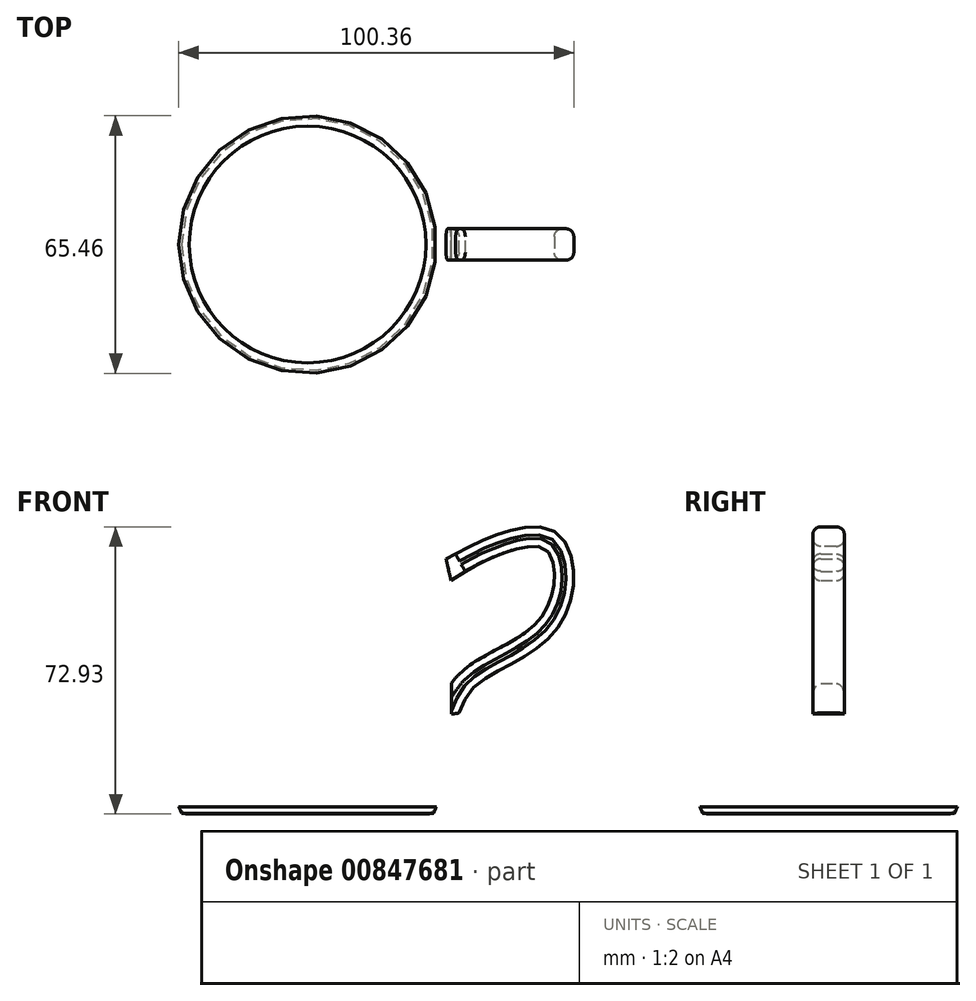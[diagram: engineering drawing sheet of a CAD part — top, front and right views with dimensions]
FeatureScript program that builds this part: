
annotation { "Feature Type Name" : "Feature", "Feature Type Description" : "" }
export const myFeature = defineFeature(function(context is Context, id is Id, definition is map)
    precondition{}
    {
        {
            var Q0;
            Q0=qCreatedBy(makeId("Front.planeOp"),FACE);
            var sketch = newSketch(context, id + "F0", { "sketchPlane" : qUnion([Q0])});
            skFitSpline(sketch, "E0", {"points": [v(0, 3) * mm, v(11.69, 2.8) * mm, v(27, 0) * mm, v(32, 0) * mm], "startDerivative": vector(30.02, 0) * mm, "endDerivative": vector(16.65, 1.68) * mm});
            skFitSpline(sketch, "E1", {"points": [v(32, 0) * mm, v(37.17, 14.97) * mm, v(38.39, 37.94) * mm, v(37.4, 75) * mm], "startDerivative": vector(17.24, 38.39) * mm, "endDerivative": vector(0, 26.02) * mm});
            skFitSpline(sketch, "E2.0", {"points": [v(27.44, 2.05) * mm, v(27.77, 2.79) * mm, v(28.54, 4.57) * mm, v(29.8, 7.84) * mm, v(30.84, 10.85) * mm, v(31.58, 13.29) * mm, v(31.99, 14.8) * mm, v(32.28, 15.97) * mm, v(32.53, 17.13) * mm, v(32.91, 19.12) * mm, v(33.28, 21.97) * mm, v(33.5, 25.7) * mm, v(33.54, 29.28) * mm, v(33.5, 32.54) * mm, v(33.45, 35.2) * mm, v(33.38, 38.1) * mm, v(33.3, 41.26) * mm, v(33.21, 44.6) * mm, v(33.08, 49.2) * mm, v(32.92, 55.1) * mm, v(32.72, 61.86) * mm, v(32.58, 66.83) * mm, v(32.5, 70.15) * mm, v(32.45, 72.25) * mm, v(32.42, 73.63) * mm, v(32.41, 74.5) * mm, v(32.4, 74.84) * mm, v(32.4, 75) * mm]});
            skFitSpline(sketch, "E2.1", {"points": [v(0, 8) * mm, v(0.57, 8) * mm, v(1.76, 8.02) * mm, v(3.68, 8.07) * mm, v(5.76, 8.1) * mm, v(7.64, 8.1) * mm, v(9.23, 8.03) * mm, v(10.46, 7.95) * mm, v(11.74, 7.83) * mm, v(13.5, 7.62) * mm, v(15.72, 7.27) * mm, v(18.35, 6.76) * mm, v(20.9, 6.23) * mm, v(23.29, 5.72) * mm, v(25.1, 5.36) * mm, v(26.36, 5.14) * mm, v(27.07, 5.03) * mm, v(27.57, 4.97) * mm, v(28.03, 4.92) * mm, v(28.55, 4.87) * mm, v(29.11, 4.85) * mm, v(29.79, 4.84) * mm, v(30.54, 4.88) * mm, v(31.16, 4.94) * mm, v(31.5, 4.97) * mm]});
            skLineSegment(sketch, "E3", {"start": v(0, 3) * mm, "end": v(0, 8) * mm});
            skLineSegment(sketch, "E4", {"start": v(35.44, 75) * mm, "end": v(34.43, 75) * mm});
            skArc(sketch, "E5.filletArc", {"start": v(30.07, -0.14) * mm, "mid": v(31.67, 0.38) * mm, "end": v(32.73, 1.69) * mm});
            skPoint(sketch, "E6.visualSharp", {"position": v(28.64, 4.87) * mm});
            skArc(sketch, "E6.filletArc", {"start": v(26.19, 5.17) * mm, "mid": v(28.19, 5.53) * mm, "end": v(29.5, 7.08) * mm});
            skArc(sketch, "E7.filletArc", {"start": v(37.43, 73.04) * mm, "mid": v(36.84, 74.43) * mm, "end": v(35.44, 75) * mm});
            skPoint(sketch, "E8.visualSharp", {"position": v(32.4, 75) * mm});
            skArc(sketch, "E8.filletArc", {"start": v(34.43, 75) * mm, "mid": v(33, 74.4) * mm, "end": v(32.44, 72.96) * mm});
            skSolve(sketch);
        }
        {
            var Q0;
            Q0=makeQuery(id+"F0.imprint","IMPRINT",FACE,{"disambiguationData":[TD([[makeQuery(id+"F0.imprint","IMPRINT",EDGE,{"derivedFrom":sQuery(id+"F0.wireOp",EDGE,"E0")}),1.0]])]});
            var Q1;
            Q1=sQuery(id+"F0.wireOp",EDGE,"E3");
            revolve(context, id + "F1", {"surfaceOperationType" : NewSurfaceOperationType.NEW, "entities" : qUnion([Q0]), "axis" : qUnion([Q1]), "revolveType" : RevolveType.FULL});
        }
        {
            var Q0;
            Q0=qCreatedBy(makeId("Front.planeOp"),FACE);
            var sketch = newSketch(context, id + "F2", { "sketchPlane" : qUnion([Q0])});
            skFitSpline(sketch, "E9", {"points": [v(38.47, 25.48) * mm, v(43.4, 33.01) * mm, v(64.12, 47.88) * mm, v(63.7, 70.9) * mm, v(37.61, 65.87) * mm], "startDerivative": vector(18.11, 46.75) * mm, "endDerivative": vector(-100.56, -56.33) * mm});
            skFitSpline(sketch, "E10.0", {"points": [v(33.8, 27.28) * mm, v(33.99, 27.76) * mm, v(34.39, 28.8) * mm, v(35.15, 30.57) * mm, v(36.2, 32.5) * mm, v(37.4, 34.14) * mm, v(38.57, 35.42) * mm, v(39.4, 36.2) * mm, v(40.1, 36.8) * mm, v(40.86, 37.38) * mm, v(41.81, 38.05) * mm, v(43, 38.8) * mm, v(44.6, 39.74) * mm, v(46.67, 40.86) * mm, v(49.2, 42.2) * mm, v(51.68, 43.58) * mm, v(54.05, 45.04) * mm, v(56.2, 46.6) * mm, v(57.77, 47.98) * mm, v(58.84, 49.14) * mm, v(59.56, 50.04) * mm, v(60.18, 50.97) * mm, v(60.74, 51.98) * mm, v(61.24, 53.08) * mm, v(61.82, 54.62) * mm, v(62.34, 56.66) * mm, v(62.65, 59.15) * mm, v(62.63, 61.55) * mm, v(62.3, 63.69) * mm, v(61.83, 65.13) * mm, v(61.39, 66) * mm, v(61.05, 66.5) * mm, v(60.79, 66.81) * mm, v(60.6, 67) * mm, v(60.4, 67.14) * mm, v(60.14, 67.3) * mm, v(59.73, 67.48) * mm, v(59.2, 67.64) * mm, v(58.28, 67.79) * mm, v(56.78, 67.81) * mm, v(54.52, 67.5) * mm, v(51.91, 66.84) * mm, v(49.08, 65.86) * mm, v(45.1, 64.2) * mm, v(42.05, 62.62) * mm, v(40.06, 61.5) * mm]});
            skLineSegment(sketch, "E11", {"start": v(37.61, 65.87) * mm, "end": v(35.17, 64.65) * mm});
            skLineSegment(sketch, "E12", {"start": v(35.17, 64.65) * mm, "end": v(36.43, 59.1) * mm});
            skLineSegment(sketch, "E13", {"start": v(36.43, 59.1) * mm, "end": v(40.06, 61.5) * mm});
            skLineSegment(sketch, "E14", {"start": v(38.45, 35.27) * mm, "end": v(36.53, 34.5) * mm});
            skLineSegment(sketch, "E15", {"start": v(36.53, 34.5) * mm, "end": v(36.53, 25.19) * mm});
            skLineSegment(sketch, "E16", {"start": v(36.53, 25.19) * mm, "end": v(38.47, 25.48) * mm});
            skSolve(sketch);
        }
        {
            var Q0;
            Q0=makeQuery(id+"F2.imprint","IMPRINT",FACE,{"disambiguationData":[TD([[makeQuery(id+"F2.imprint","IMPRINT",EDGE,{"derivedFrom":sQuery(id+"F2.wireOp",EDGE,"E9")}),1.0]])]});
            extrude(context, id + "F3", {"entities" : qUnion([Q0]), "operationType" : NewBodyOperationType.ADD, "depth" : 4 * mm, "offsetDistance" : 25 * mm, "hasSecondDirection" : true, "secondDirectionOppositeDirection" : true, "secondDirectionDepth" : 4 * mm});
        }
        {
            var Q0;
            Q0=makeQuery(id+"F3.opExtrude","CAP_EDGE",EDGE,{"disambiguationData":[OSD([sQuery(id+"F2.wireOp",EDGE,"E9")])],"isStart":false});
            var Q1;
            Q1=makeQuery(id+"F3.opExtrude","CAP_EDGE",EDGE,{"disambiguationData":[OSD([sQuery(id+"F2.wireOp",EDGE,"E10.0")])],"isStart":false});
            var Q2;
            Q2=makeQuery(id+"F3.opExtrude","CAP_EDGE",EDGE,{"disambiguationData":[OSD([sQuery(id+"F2.wireOp",EDGE,"E13")])],"isStart":false});
            var Q3;
            Q3=makeQuery(id+"F3.opExtrude","CAP_EDGE",EDGE,{"disambiguationData":[OSD([sQuery(id+"F2.wireOp",EDGE,"E9")])],"isStart":true});
            var Q4;
            Q4=makeQuery(id+"F3.opExtrude","CAP_EDGE",EDGE,{"disambiguationData":[OSD([sQuery(id+"F2.wireOp",EDGE,"E10.0")])],"isStart":true});
            var Q5;
            Q5=makeQuery(id+"F3.opExtrude","CAP_EDGE",EDGE,{"disambiguationData":[OSD([sQuery(id+"F2.wireOp",EDGE,"E13")])],"isStart":true});
            fillet(context, id + "F4", {"entities" : qUnion([Q0, Q1, Q2, Q3, Q4, Q5]), "radius" : 2 * mm, "tangentPropagation" : true, "allowEdgeOverflow" : false});
        }
    });
